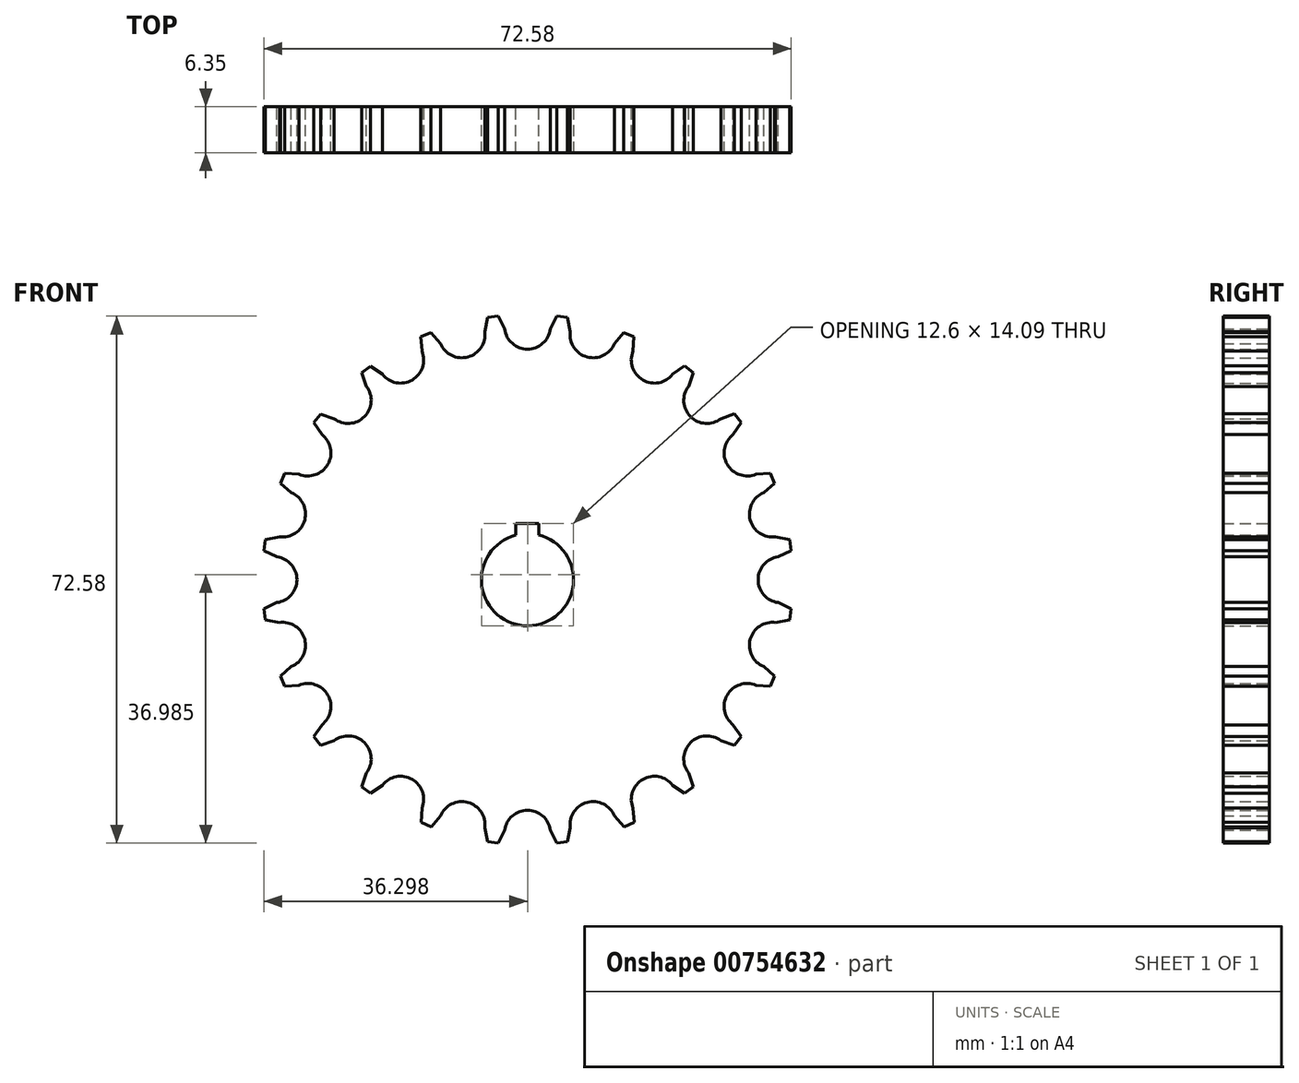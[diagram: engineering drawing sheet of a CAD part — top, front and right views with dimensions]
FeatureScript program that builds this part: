
annotation { "Feature Type Name" : "Feature", "Feature Type Description" : "" }
export const myFeature = defineFeature(function(context is Context, id is Id, definition is map)
    precondition{}
    {
        {
            var Q0;
            Q0=qCreatedBy(makeId("Front.planeOp"),FACE);
            var sketch = newSketch(context, id + "F0", { "sketchPlane" : qUnion([Q0])});
            skArc(sketch, "E0", {"start": v(-3.15, 34.51) * mm, "mid": v(0, 31.75) * mm, "end": v(3.15, 34.51) * mm});
            skPoint(sketch, "E1.center", {"position": v(0, 0) * mm});
            skLineSegment(sketch, "E2", {"start": v(3.15, 34.51) * mm, "end": v(4, 36.3) * mm});
            skLineSegment(sketch, "E3", {"start": v(5.9, 34.15) * mm, "end": v(5.5, 36.1) * mm});
            skLineSegment(sketch, "E4", {"start": v(5.5, 36.1) * mm, "end": v(4, 36.3) * mm});
            skPoint(sketch, "E5.end.orphan", {"position": v(3.4, 36.35) * mm});
            skPoint(sketch, "E6.orphan", {"position": v(6.13, 36) * mm});
            skArc(sketch, "E7.1.0", {"start": v(-11.97, 32.52) * mm, "mid": v(-8.22, 30.67) * mm, "end": v(-5.9, 34.15) * mm});
            skPoint(sketch, "E7.1.1", {"position": v(-6.13, 36) * mm});
            skLineSegment(sketch, "E7.1.2", {"start": v(-5.9, 34.15) * mm, "end": v(-5.52, 36.1) * mm});
            skLineSegment(sketch, "E7.1.3", {"start": v(-3.15, 34.51) * mm, "end": v(-4.02, 36.3) * mm});
            skLineSegment(sketch, "E7.1.4", {"start": v(-4.02, 36.3) * mm, "end": v(-5.52, 36.1) * mm});
            skArc(sketch, "E7.2.0", {"start": v(-19.98, 28.31) * mm, "mid": v(-15.87, 27.5) * mm, "end": v(-14.53, 31.46) * mm});
            skPoint(sketch, "E7.2.1", {"position": v(-15.24, 33.18) * mm});
            skLineSegment(sketch, "E7.2.2", {"start": v(-14.53, 31.46) * mm, "end": v(-14.67, 33.44) * mm});
            skLineSegment(sketch, "E7.2.3", {"start": v(-11.97, 32.52) * mm, "end": v(-13.28, 34.01) * mm});
            skLineSegment(sketch, "E7.2.4", {"start": v(-13.28, 34.01) * mm, "end": v(-14.67, 33.44) * mm});
            skArc(sketch, "E7.3.0", {"start": v(-26.63, 22.18) * mm, "mid": v(-22.45, 22.45) * mm, "end": v(-22.18, 26.63) * mm});
            skPoint(sketch, "E7.3.1", {"position": v(-23.3, 28.1) * mm});
            skLineSegment(sketch, "E7.3.2", {"start": v(-22.18, 26.63) * mm, "end": v(-22.83, 28.5) * mm});
            skLineSegment(sketch, "E7.3.3", {"start": v(-19.98, 28.31) * mm, "end": v(-21.63, 29.42) * mm});
            skLineSegment(sketch, "E7.3.4", {"start": v(-21.63, 29.42) * mm, "end": v(-22.83, 28.5) * mm});
            skArc(sketch, "E7.4.0", {"start": v(-31.46, 14.53) * mm, "mid": v(-27.5, 15.88) * mm, "end": v(-28.31, 19.98) * mm});
            skPoint(sketch, "E7.4.1", {"position": v(-29.79, 21.11) * mm});
            skLineSegment(sketch, "E7.4.2", {"start": v(-28.31, 19.98) * mm, "end": v(-29.43, 21.62) * mm});
            skLineSegment(sketch, "E7.4.3", {"start": v(-26.63, 22.18) * mm, "end": v(-28.5, 22.82) * mm});
            skLineSegment(sketch, "E7.4.4", {"start": v(-28.5, 22.82) * mm, "end": v(-29.43, 21.62) * mm});
            skArc(sketch, "E7.5.0", {"start": v(-34.15, 5.9) * mm, "mid": v(-30.67, 8.22) * mm, "end": v(-32.52, 11.97) * mm});
            skPoint(sketch, "E7.5.1", {"position": v(-34.24, 12.68) * mm});
            skLineSegment(sketch, "E7.5.2", {"start": v(-32.52, 11.97) * mm, "end": v(-34.02, 13.27) * mm});
            skLineSegment(sketch, "E7.5.3", {"start": v(-31.46, 14.53) * mm, "end": v(-33.44, 14.66) * mm});
            skLineSegment(sketch, "E7.5.4", {"start": v(-33.44, 14.66) * mm, "end": v(-34.02, 13.27) * mm});
            skArc(sketch, "E7.6.0", {"start": v(-34.51, -3.15) * mm, "mid": v(-31.75, 0) * mm, "end": v(-34.51, 3.15) * mm});
            skPoint(sketch, "E7.6.1", {"position": v(-36.35, 3.4) * mm});
            skLineSegment(sketch, "E7.6.2", {"start": v(-34.51, 3.15) * mm, "end": v(-36.3, 4) * mm});
            skLineSegment(sketch, "E7.6.3", {"start": v(-34.15, 5.9) * mm, "end": v(-36.1, 5.5) * mm});
            skLineSegment(sketch, "E7.6.4", {"start": v(-36.1, 5.5) * mm, "end": v(-36.3, 4) * mm});
            skArc(sketch, "E7.7.0", {"start": v(-32.52, -11.97) * mm, "mid": v(-30.67, -8.22) * mm, "end": v(-34.15, -5.9) * mm});
            skPoint(sketch, "E7.7.1", {"position": v(-36, -6.13) * mm});
            skLineSegment(sketch, "E7.7.2", {"start": v(-34.15, -5.9) * mm, "end": v(-36.1, -5.52) * mm});
            skLineSegment(sketch, "E7.7.3", {"start": v(-34.51, -3.15) * mm, "end": v(-36.3, -4.02) * mm});
            skLineSegment(sketch, "E7.7.4", {"start": v(-36.3, -4.02) * mm, "end": v(-36.1, -5.52) * mm});
            skArc(sketch, "E7.8.0", {"start": v(-28.31, -19.98) * mm, "mid": v(-27.5, -15.87) * mm, "end": v(-31.46, -14.53) * mm});
            skPoint(sketch, "E7.8.1", {"position": v(-33.18, -15.24) * mm});
            skLineSegment(sketch, "E7.8.2", {"start": v(-31.46, -14.53) * mm, "end": v(-33.44, -14.67) * mm});
            skLineSegment(sketch, "E7.8.3", {"start": v(-32.52, -11.97) * mm, "end": v(-34.01, -13.28) * mm});
            skLineSegment(sketch, "E7.8.4", {"start": v(-34.01, -13.28) * mm, "end": v(-33.44, -14.67) * mm});
            skArc(sketch, "E7.9.0", {"start": v(-22.18, -26.63) * mm, "mid": v(-22.45, -22.45) * mm, "end": v(-26.63, -22.18) * mm});
            skPoint(sketch, "E7.9.1", {"position": v(-28.1, -23.3) * mm});
            skLineSegment(sketch, "E7.9.2", {"start": v(-26.63, -22.18) * mm, "end": v(-28.5, -22.83) * mm});
            skLineSegment(sketch, "E7.9.3", {"start": v(-28.31, -19.98) * mm, "end": v(-29.42, -21.63) * mm});
            skLineSegment(sketch, "E7.9.4", {"start": v(-29.42, -21.63) * mm, "end": v(-28.5, -22.83) * mm});
            skArc(sketch, "E7.10.0", {"start": v(-14.53, -31.46) * mm, "mid": v(-15.88, -27.5) * mm, "end": v(-19.98, -28.31) * mm});
            skPoint(sketch, "E7.10.1", {"position": v(-21.11, -29.79) * mm});
            skLineSegment(sketch, "E7.10.2", {"start": v(-19.98, -28.31) * mm, "end": v(-21.62, -29.43) * mm});
            skLineSegment(sketch, "E7.10.3", {"start": v(-22.18, -26.63) * mm, "end": v(-22.82, -28.5) * mm});
            skLineSegment(sketch, "E7.10.4", {"start": v(-22.82, -28.5) * mm, "end": v(-21.62, -29.43) * mm});
            skArc(sketch, "E7.11.0", {"start": v(-5.9, -34.15) * mm, "mid": v(-8.22, -30.67) * mm, "end": v(-11.97, -32.52) * mm});
            skPoint(sketch, "E7.11.1", {"position": v(-12.68, -34.24) * mm});
            skLineSegment(sketch, "E7.11.2", {"start": v(-11.97, -32.52) * mm, "end": v(-13.27, -34.02) * mm});
            skLineSegment(sketch, "E7.11.3", {"start": v(-14.53, -31.46) * mm, "end": v(-14.66, -33.44) * mm});
            skLineSegment(sketch, "E7.11.4", {"start": v(-14.66, -33.44) * mm, "end": v(-13.27, -34.02) * mm});
            skArc(sketch, "E7.12.0", {"start": v(3.15, -34.51) * mm, "mid": v(0, -31.75) * mm, "end": v(-3.15, -34.51) * mm});
            skPoint(sketch, "E7.12.1", {"position": v(-3.4, -36.35) * mm});
            skLineSegment(sketch, "E7.12.2", {"start": v(-3.15, -34.51) * mm, "end": v(-4, -36.3) * mm});
            skLineSegment(sketch, "E7.12.3", {"start": v(-5.9, -34.15) * mm, "end": v(-5.5, -36.1) * mm});
            skLineSegment(sketch, "E7.12.4", {"start": v(-5.5, -36.1) * mm, "end": v(-4, -36.3) * mm});
            skArc(sketch, "E7.13.0", {"start": v(11.97, -32.52) * mm, "mid": v(8.22, -30.67) * mm, "end": v(5.9, -34.15) * mm});
            skPoint(sketch, "E7.13.1", {"position": v(6.13, -36) * mm});
            skLineSegment(sketch, "E7.13.2", {"start": v(5.9, -34.15) * mm, "end": v(5.52, -36.1) * mm});
            skLineSegment(sketch, "E7.13.3", {"start": v(3.15, -34.51) * mm, "end": v(4.02, -36.3) * mm});
            skLineSegment(sketch, "E7.13.4", {"start": v(4.02, -36.3) * mm, "end": v(5.52, -36.1) * mm});
            skArc(sketch, "E7.14.0", {"start": v(19.98, -28.31) * mm, "mid": v(15.87, -27.5) * mm, "end": v(14.53, -31.46) * mm});
            skPoint(sketch, "E7.14.1", {"position": v(15.24, -33.18) * mm});
            skLineSegment(sketch, "E7.14.2", {"start": v(14.53, -31.46) * mm, "end": v(14.67, -33.44) * mm});
            skLineSegment(sketch, "E7.14.3", {"start": v(11.97, -32.52) * mm, "end": v(13.28, -34.01) * mm});
            skLineSegment(sketch, "E7.14.4", {"start": v(13.28, -34.01) * mm, "end": v(14.67, -33.44) * mm});
            skArc(sketch, "E7.15.0", {"start": v(26.63, -22.18) * mm, "mid": v(22.45, -22.45) * mm, "end": v(22.18, -26.63) * mm});
            skPoint(sketch, "E7.15.1", {"position": v(23.3, -28.1) * mm});
            skLineSegment(sketch, "E7.15.2", {"start": v(22.18, -26.63) * mm, "end": v(22.83, -28.5) * mm});
            skLineSegment(sketch, "E7.15.3", {"start": v(19.98, -28.31) * mm, "end": v(21.63, -29.42) * mm});
            skLineSegment(sketch, "E7.15.4", {"start": v(21.63, -29.42) * mm, "end": v(22.83, -28.5) * mm});
            skArc(sketch, "E7.16.0", {"start": v(31.46, -14.53) * mm, "mid": v(27.5, -15.88) * mm, "end": v(28.31, -19.98) * mm});
            skPoint(sketch, "E7.16.1", {"position": v(29.79, -21.11) * mm});
            skLineSegment(sketch, "E7.16.2", {"start": v(28.31, -19.98) * mm, "end": v(29.43, -21.62) * mm});
            skLineSegment(sketch, "E7.16.3", {"start": v(26.63, -22.18) * mm, "end": v(28.5, -22.82) * mm});
            skLineSegment(sketch, "E7.16.4", {"start": v(28.5, -22.82) * mm, "end": v(29.43, -21.62) * mm});
            skArc(sketch, "E7.17.0", {"start": v(34.15, -5.9) * mm, "mid": v(30.67, -8.22) * mm, "end": v(32.52, -11.97) * mm});
            skPoint(sketch, "E7.17.1", {"position": v(34.24, -12.68) * mm});
            skLineSegment(sketch, "E7.17.2", {"start": v(32.52, -11.97) * mm, "end": v(34.02, -13.27) * mm});
            skLineSegment(sketch, "E7.17.3", {"start": v(31.46, -14.53) * mm, "end": v(33.44, -14.66) * mm});
            skLineSegment(sketch, "E7.17.4", {"start": v(33.44, -14.66) * mm, "end": v(34.02, -13.27) * mm});
            skArc(sketch, "E7.18.0", {"start": v(34.51, 3.15) * mm, "mid": v(31.75, 0) * mm, "end": v(34.51, -3.15) * mm});
            skPoint(sketch, "E7.18.1", {"position": v(36.35, -3.4) * mm});
            skLineSegment(sketch, "E7.18.2", {"start": v(34.51, -3.15) * mm, "end": v(36.3, -4) * mm});
            skLineSegment(sketch, "E7.18.3", {"start": v(34.15, -5.9) * mm, "end": v(36.1, -5.5) * mm});
            skLineSegment(sketch, "E7.18.4", {"start": v(36.1, -5.5) * mm, "end": v(36.3, -4) * mm});
            skArc(sketch, "E7.19.0", {"start": v(32.52, 11.97) * mm, "mid": v(30.67, 8.22) * mm, "end": v(34.15, 5.9) * mm});
            skPoint(sketch, "E7.19.1", {"position": v(36, 6.13) * mm});
            skLineSegment(sketch, "E7.19.2", {"start": v(34.15, 5.9) * mm, "end": v(36.1, 5.52) * mm});
            skLineSegment(sketch, "E7.19.3", {"start": v(34.51, 3.15) * mm, "end": v(36.3, 4.02) * mm});
            skLineSegment(sketch, "E7.19.4", {"start": v(36.3, 4.02) * mm, "end": v(36.1, 5.52) * mm});
            skArc(sketch, "E7.20.0", {"start": v(28.31, 19.98) * mm, "mid": v(27.5, 15.88) * mm, "end": v(31.46, 14.53) * mm});
            skPoint(sketch, "E7.20.1", {"position": v(33.18, 15.24) * mm});
            skLineSegment(sketch, "E7.20.2", {"start": v(31.46, 14.53) * mm, "end": v(33.44, 14.67) * mm});
            skLineSegment(sketch, "E7.20.3", {"start": v(32.52, 11.97) * mm, "end": v(34.01, 13.28) * mm});
            skLineSegment(sketch, "E7.20.4", {"start": v(34.01, 13.28) * mm, "end": v(33.44, 14.67) * mm});
            skArc(sketch, "E7.21.0", {"start": v(22.18, 26.63) * mm, "mid": v(22.45, 22.45) * mm, "end": v(26.63, 22.18) * mm});
            skPoint(sketch, "E7.21.1", {"position": v(28.1, 23.3) * mm});
            skLineSegment(sketch, "E7.21.2", {"start": v(26.63, 22.18) * mm, "end": v(28.5, 22.83) * mm});
            skLineSegment(sketch, "E7.21.3", {"start": v(28.31, 19.98) * mm, "end": v(29.42, 21.63) * mm});
            skLineSegment(sketch, "E7.21.4", {"start": v(29.42, 21.63) * mm, "end": v(28.5, 22.83) * mm});
            skArc(sketch, "E7.22.0", {"start": v(14.53, 31.46) * mm, "mid": v(15.88, 27.5) * mm, "end": v(19.98, 28.31) * mm});
            skPoint(sketch, "E7.22.1", {"position": v(21.11, 29.79) * mm});
            skLineSegment(sketch, "E7.22.2", {"start": v(19.98, 28.31) * mm, "end": v(21.62, 29.43) * mm});
            skLineSegment(sketch, "E7.22.3", {"start": v(22.18, 26.63) * mm, "end": v(22.82, 28.5) * mm});
            skLineSegment(sketch, "E7.22.4", {"start": v(22.82, 28.5) * mm, "end": v(21.62, 29.43) * mm});
            skArc(sketch, "E7.23.0", {"start": v(5.9, 34.15) * mm, "mid": v(8.22, 30.67) * mm, "end": v(11.97, 32.52) * mm});
            skPoint(sketch, "E7.23.1", {"position": v(12.68, 34.24) * mm});
            skLineSegment(sketch, "E7.23.2", {"start": v(11.97, 32.52) * mm, "end": v(13.27, 34.02) * mm});
            skLineSegment(sketch, "E7.23.3", {"start": v(14.53, 31.46) * mm, "end": v(14.66, 33.44) * mm});
            skLineSegment(sketch, "E7.23.4", {"start": v(14.66, 33.44) * mm, "end": v(13.27, 34.02) * mm});
            skPoint(sketch, "E8.orphan", {"position": v(-2.8, 36.4) * mm});
            skPoint(sketch, "E9.orphan", {"position": v(6.7, 35.9) * mm});
            skPoint(sketch, "E10.orphan", {"position": v(15.77, 32.93) * mm});
            skPoint(sketch, "E11.orphan", {"position": v(23.76, 27.73) * mm});
            skPoint(sketch, "E12.orphan", {"position": v(30.12, 20.64) * mm});
            skPoint(sketch, "E13.orphan", {"position": v(34.44, 12.14) * mm});
            skPoint(sketch, "E14.orphan", {"position": v(36.4, 2.8) * mm});
            skPoint(sketch, "E15.orphan", {"position": v(35.9, -6.7) * mm});
            skPoint(sketch, "E16.orphan", {"position": v(32.93, -15.77) * mm});
            skPoint(sketch, "E17.orphan", {"position": v(27.73, -23.76) * mm});
            skPoint(sketch, "E18.orphan", {"position": v(20.64, -30.12) * mm});
            skPoint(sketch, "E19.orphan", {"position": v(12.14, -34.44) * mm});
            skPoint(sketch, "E20.orphan", {"position": v(2.8, -36.4) * mm});
            skPoint(sketch, "E21.orphan", {"position": v(-6.7, -35.9) * mm});
            skPoint(sketch, "E22.orphan", {"position": v(-15.77, -32.93) * mm});
            skPoint(sketch, "E23.orphan", {"position": v(-23.76, -27.73) * mm});
            skPoint(sketch, "E24.orphan", {"position": v(-30.12, -20.64) * mm});
            skPoint(sketch, "E25.orphan", {"position": v(-34.44, -12.14) * mm});
            skPoint(sketch, "E26.orphan", {"position": v(-36.4, -2.8) * mm});
            skPoint(sketch, "E27.orphan", {"position": v(-35.9, 6.7) * mm});
            skPoint(sketch, "E28.orphan", {"position": v(-32.93, 15.77) * mm});
            skPoint(sketch, "E29.orphan", {"position": v(-27.73, 23.76) * mm});
            skPoint(sketch, "E30.orphan", {"position": v(-20.64, 30.12) * mm});
            skPoint(sketch, "E31.orphan", {"position": v(-12.14, 34.44) * mm});
            skArc(sketch, "E32", {"start": v(-1.65, 6.13) * mm, "mid": v(0.07, -6.35) * mm, "end": v(1.52, 6.16) * mm});
            skLineSegment(sketch, "E33", {"start": v(1.52, 6.16) * mm, "end": v(1.52, 7.74) * mm});
            skLineSegment(sketch, "E34", {"start": v(1.52, 7.74) * mm, "end": v(-1.65, 7.74) * mm});
            skLineSegment(sketch, "E35", {"start": v(-1.65, 7.74) * mm, "end": v(-1.65, 6.13) * mm});
            skSolve(sketch);
        }
        {
            var Q0;
            Q0=makeQuery(id+"F0.imprint","IMPRINT",FACE,{"disambiguationData":[TD([[makeQuery(id+"F0.imprint","IMPRINT",EDGE,{"derivedFrom":sQuery(id+"F0.wireOp",EDGE,"E0")}),-1.0]])]});
            extrude(context, id + "F1", {"entities" : qUnion([Q0]), "depth" : 6.35 * mm, "offsetDistance" : 25.4 * mm});
        }
    });
